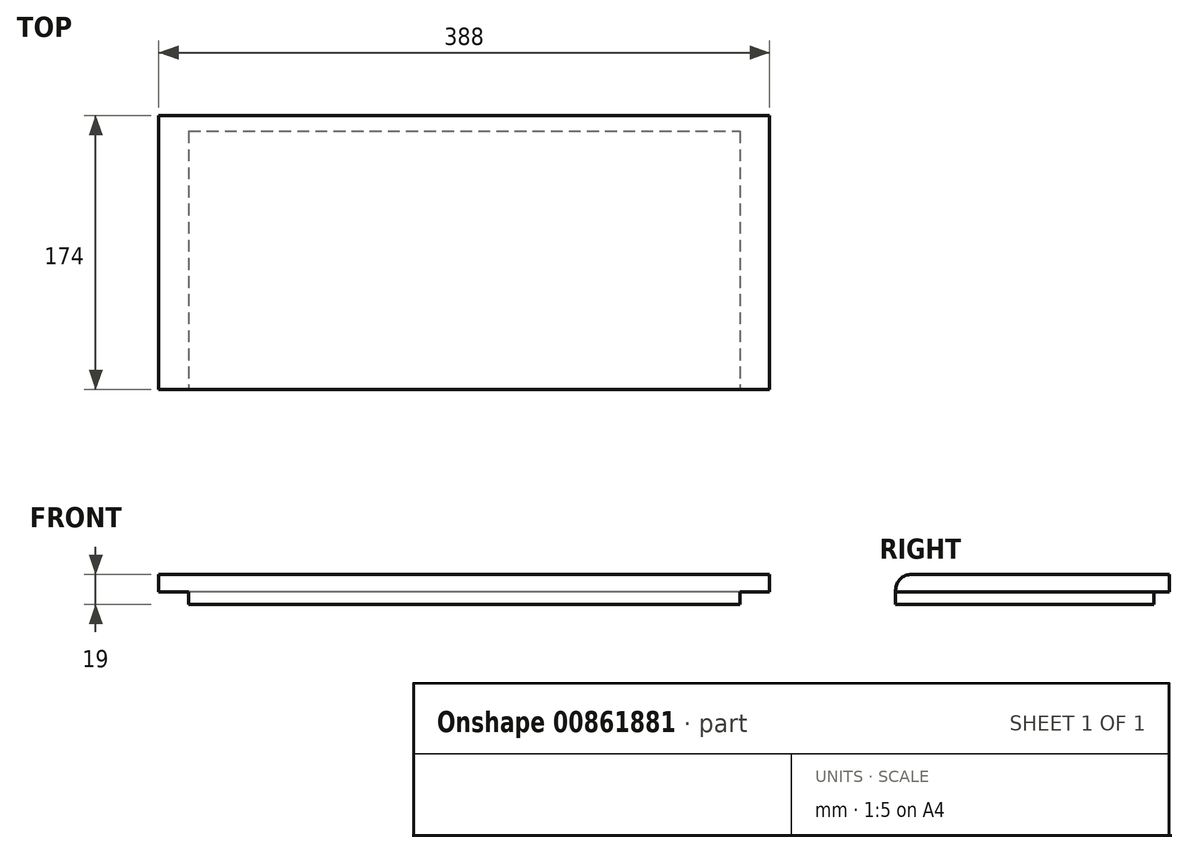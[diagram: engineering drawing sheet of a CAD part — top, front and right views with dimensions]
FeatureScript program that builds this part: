
annotation { "Feature Type Name" : "Feature", "Feature Type Description" : "" }
export const myFeature = defineFeature(function(context is Context, id is Id, definition is map)
    precondition{}
    {
        {
            var Q0;
            Q0=qCreatedBy(makeId("Top.planeOp"),FACE);
            var sketch = newSketch(context, id + "F0", { "sketchPlane" : qUnion([Q0])});
            skLineSegment(sketch, "E0.bottom", {"start": v(-194, 87) * mm, "end": v(194, 87) * mm});
            skLineSegment(sketch, "E0.top", {"start": v(-194, -87) * mm, "end": v(194, -87) * mm});
            skLineSegment(sketch, "E0.left", {"start": v(-194, 87) * mm, "end": v(-194, -87) * mm});
            skLineSegment(sketch, "E0.right", {"start": v(194, 87) * mm, "end": v(194, -87) * mm});
            skPoint(sketch, "E0.middle", {"position": v(0, 0) * mm});
            skSolve(sketch);
        }
        {
            var Q0;
            Q0=makeQuery(id+"F0.imprint","IMPRINT",FACE,{"disambiguationData":[TD([[makeQuery(id+"F0.imprint","IMPRINT",EDGE,{"derivedFrom":sQuery(id+"F0.wireOp",EDGE,"E0.bottom")}),-1.0]])]});
            extrude(context, id + "F1", {"entities" : qUnion([Q0]), "depth" : 19 * mm, "offsetDistance" : 25 * mm});
        }
        {
            var Q0;
            Q0=makeQuery(id+"F1.opExtrude","SWEPT_FACE",FACE,{"disambiguationData":[OSD([sQuery(id+"F0.wireOp",EDGE,"E0.top")])]});
            var sketch = newSketch(context, id + "F2", { "sketchPlane" : qUnion([Q0])});
            skLineSegment(sketch, "E1", {"start": v(-194, 0) * mm, "end": v(-194, 8) * mm});
            skLineSegment(sketch, "E2", {"start": v(-194, 8) * mm, "end": v(-175, 8) * mm});
            skLineSegment(sketch, "E3", {"start": v(-175, 8) * mm, "end": v(-175, 0) * mm});
            skLineSegment(sketch, "E4", {"start": v(194, 0) * mm, "end": v(194, 8) * mm});
            skLineSegment(sketch, "E5", {"start": v(194, 8) * mm, "end": v(175, 8) * mm});
            skLineSegment(sketch, "E6", {"start": v(175, 8) * mm, "end": v(175, 0) * mm});
            skSolve(sketch);
        }
        {
            var Q0;
            {var subQ0=sQuery(id+"F2.wireOp",EDGE,"E4");Q0=makeQuery(id+"F2.imprint","IMPRINT",FACE,{"disambiguationData":[TD([[makeQuery(id+"F2.imprint","IMPRINT",EDGE,{"derivedFrom":subQ0}),-1.0]])]});}
            var Q1;
            {var subQ0=sQuery(id+"F2.wireOp",EDGE,"E1");Q1=makeQuery(id+"F2.imprint","IMPRINT",FACE,{"disambiguationData":[TD([[makeQuery(id+"F2.imprint","IMPRINT",EDGE,{"derivedFrom":subQ0}),1.0]])]});}
            extrude(context, id + "F3", {"entities" : qUnion([Q0, Q1]), "operationType" : NewBodyOperationType.REMOVE, "oppositeDirection" : true, "depth" : 178 * mm, "offsetDistance" : 25 * mm});
        }
        {
            var Q0;
            Q0=makeQuery(id+"F1.opExtrude","SWEPT_FACE",FACE,{"disambiguationData":[OSD([sQuery(id+"F0.wireOp",EDGE,"E0.bottom")])]});
            var sketch = newSketch(context, id + "F4", { "sketchPlane" : qUnion([Q0])});
            skLineSegment(sketch, "E7", {"start": v(-175, 8) * mm, "end": v(175, 8) * mm});
            skSolve(sketch);
        }
        {
            var Q0;
            Q0=makeQuery(id+"F4.imprint","IMPRINT",FACE,{"disambiguationData":[TD([[makeQuery(id+"F4.imprint","IMPRINT",EDGE,{"derivedFrom":sQuery(id+"F4.wireOp",EDGE,"E7")}),-1.0]])]});
            extrude(context, id + "F5", {"entities" : qUnion([Q0]), "operationType" : NewBodyOperationType.REMOVE, "oppositeDirection" : true, "depth" : 10 * mm, "offsetDistance" : 25 * mm});
        }
        {
            var Q0;
            Q0=makeQuery(id+"F1.opExtrude","CAP_EDGE",EDGE,{"disambiguationData":[OSD([sQuery(id+"F0.wireOp",EDGE,"E0.top")])],"isStart":false});
            fillet(context, id + "F6", {"entities" : qUnion([Q0]), "radius" : 10 * mm, "tangentPropagation" : true, "allowEdgeOverflow" : false});
        }
    });
